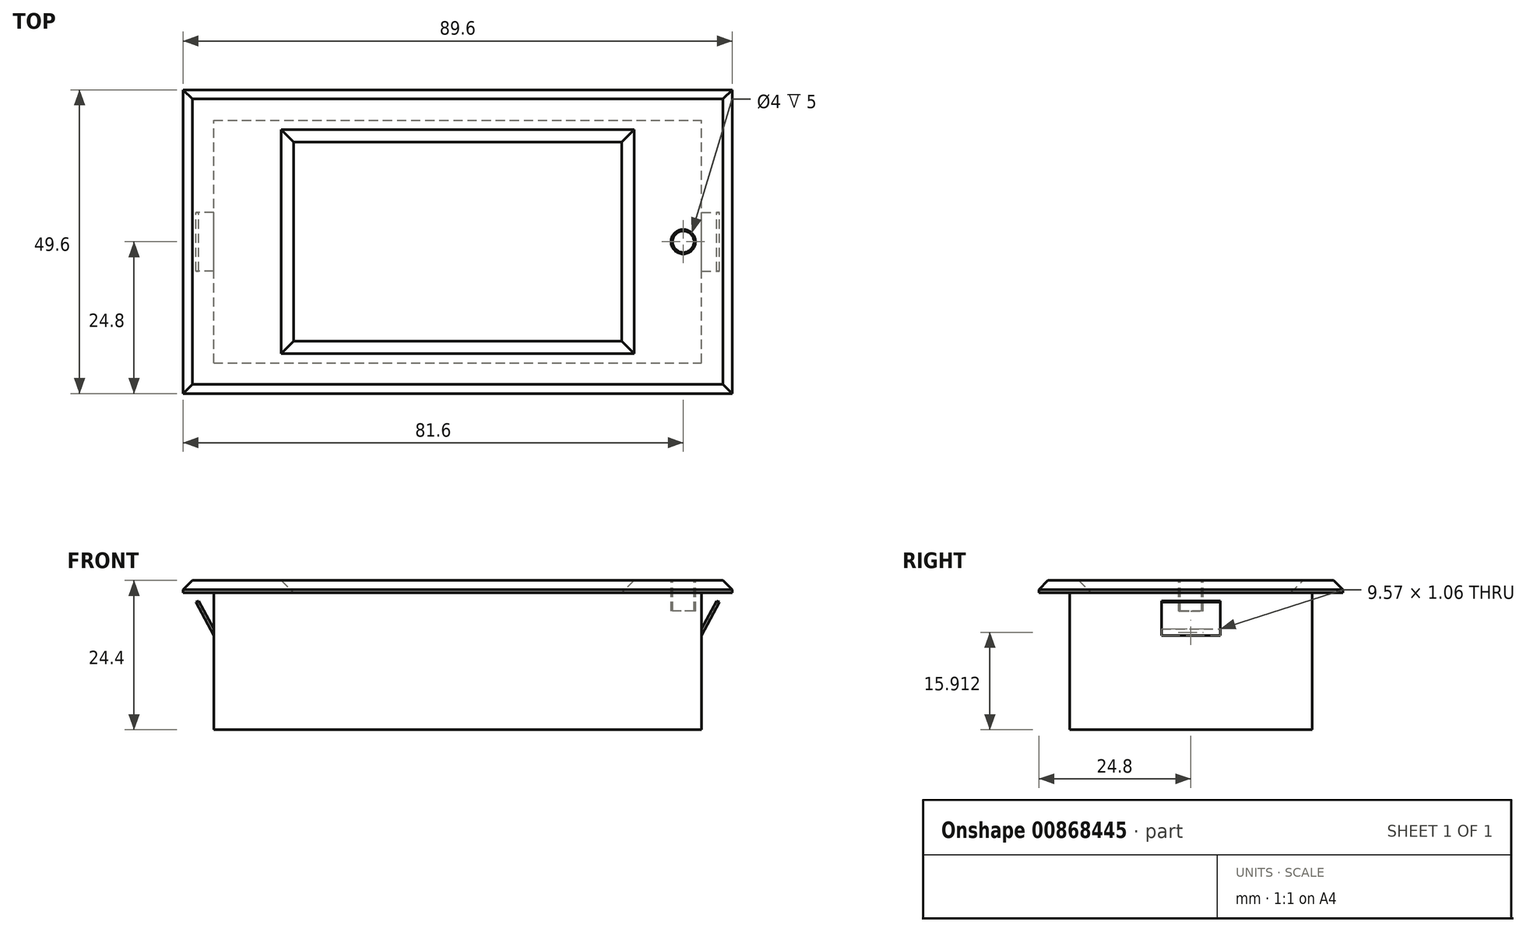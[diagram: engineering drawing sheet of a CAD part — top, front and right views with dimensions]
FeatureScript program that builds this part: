
annotation { "Feature Type Name" : "Feature", "Feature Type Description" : "" }
export const myFeature = defineFeature(function(context is Context, id is Id, definition is map)
    precondition{}
    {
        {
            var Q0;
            Q0=qCreatedBy(makeId("Top.planeOp"),FACE);
            var sketch = newSketch(context, id + "F0", { "sketchPlane" : qUnion([Q0])});
            skLineSegment(sketch, "E0.bottom", {"start": v(0, 0) * mm, "end": v(89.6, 0) * mm});
            skLineSegment(sketch, "E0.top", {"start": v(0, 49.6) * mm, "end": v(89.6, 49.6) * mm});
            skLineSegment(sketch, "E0.left", {"start": v(0, 0) * mm, "end": v(0, 49.6) * mm});
            skLineSegment(sketch, "E0.right", {"start": v(89.6, 0) * mm, "end": v(89.6, 49.6) * mm});
            skLineSegment(sketch, "E1.0", {"start": v(5, 5) * mm, "end": v(5, 44.6) * mm});
            skLineSegment(sketch, "E1.1", {"start": v(5, 5) * mm, "end": v(84.6, 5) * mm});
            skLineSegment(sketch, "E1.2", {"start": v(84.6, 5) * mm, "end": v(84.6, 44.6) * mm});
            skLineSegment(sketch, "E1.3", {"start": v(5, 44.6) * mm, "end": v(84.6, 44.6) * mm});
            skLineSegment(sketch, "E2", {"start": v(44.8, 49.6) * mm, "end": v(44.8, 0) * mm, "construction": true});
            skLineSegment(sketch, "E3", {"start": v(89.6, 24.8) * mm, "end": v(0, 24.8) * mm, "construction": true});
            skLineSegment(sketch, "E4.bottom", {"start": v(19.3, 39.8) * mm, "end": v(70.3, 39.8) * mm});
            skLineSegment(sketch, "E4.top", {"start": v(19.3, 9.8) * mm, "end": v(70.3, 9.8) * mm});
            skLineSegment(sketch, "E4.left", {"start": v(19.3, 39.8) * mm, "end": v(19.3, 9.8) * mm});
            skLineSegment(sketch, "E4.right", {"start": v(70.3, 39.8) * mm, "end": v(70.3, 9.8) * mm});
            skPoint(sketch, "E4.middle", {"position": v(44.8, 24.8) * mm});
            skSolve(sketch);
        }
        {
            var Q0;
            Q0=makeQuery(id+"F0.imprint","IMPRINT",FACE,{"disambiguationData":[TD([[makeQuery(id+"F0.imprint","IMPRINT",EDGE,{"derivedFrom":sQuery(id+"F0.wireOp",EDGE,"E1.0")}),-1.0]])]});
            var Q1;
            Q1=makeQuery(id+"F0.imprint","IMPRINT",FACE,{"disambiguationData":[TD([[makeQuery(id+"F0.imprint","IMPRINT",EDGE,{"derivedFrom":sQuery(id+"F0.wireOp",EDGE,"E4.bottom")}),-1.0]])]});
            extrude(context, id + "F1", {"entities" : qUnion([Q0, Q1]), "oppositeDirection" : true, "depth" : (24.4 - 2.05) * mm, "offsetDistance" : 25 * mm});
        }
        {
            var Q0;
            Q0=makeQuery(id+"F0.imprint","IMPRINT",FACE,{"disambiguationData":[TD([[makeQuery(id+"F0.imprint","IMPRINT",EDGE,{"derivedFrom":sQuery(id+"F0.wireOp",EDGE,"E0.bottom")}),1.0]])]});
            var Q1;
            Q1=makeQuery(id+"F0.imprint","IMPRINT",FACE,{"disambiguationData":[TD([[makeQuery(id+"F0.imprint","IMPRINT",EDGE,{"derivedFrom":sQuery(id+"F0.wireOp",EDGE,"E1.0")}),-1.0]])]});
            extrude(context, id + "F2", {"entities" : qUnion([Q0, Q1]), "operationType" : NewBodyOperationType.ADD, "depth" : 2.05 * mm, "offsetDistance" : 25 * mm});
        }
        {
            var Q0;
            Q0=qCreatedBy(makeId("Front.planeOp"),FACE);
            cPlane(context, id + "F3", {"entities" : qUnion([Q0]), "cplaneType" : CPlaneType.OFFSET, "offset" : (49.6 / 2) * mm, "oppositeDirection" : true, "width" : 150 * mm, "height" : 150 * mm});
        }
        {
            var Q0;
            Q0=qCreatedBy(id+"F3.planeOp",FACE);
            var sketch = newSketch(context, id + "F4", { "sketchPlane" : qUnion([Q0])});
            skLineSegment(sketch, "E5.0.0", {"start": v(84.6, 0) * mm, "end": v(5, 0) * mm});
            skLineSegment(sketch, "E5.0.1", {"start": v(5, 0) * mm, "end": v(5, -22.35) * mm});
            skLineSegment(sketch, "E5.0.2", {"start": v(5, -22.35) * mm, "end": v(84.6, -22.35) * mm});
            skLineSegment(sketch, "E5.0.3", {"start": v(84.6, -22.35) * mm, "end": v(84.6, 0) * mm});
            skLineSegment(sketch, "E6", {"start": v(5, -6.97) * mm, "end": v(84.6, -6.97) * mm});
            skLineSegment(sketch, "E7", {"start": v(44.8, 0) * mm, "end": v(44.8, -22.35) * mm, "construction": true});
            skLineSegment(sketch, "E8", {"start": v(5, -6.97) * mm, "end": v(2.1, -1.52) * mm});
            skLineSegment(sketch, "E9", {"start": v(2.1, -1.52) * mm, "end": v(5, -1.52) * mm, "construction": true});
            skLineSegment(sketch, "E10.0", {"start": v(5, -5.9) * mm, "end": v(2.54, -1.29) * mm});
            skLineSegment(sketch, "E11", {"start": v(2.1, -1.52) * mm, "end": v(2.54, -1.29) * mm});
            skLineSegment(sketch, "E12.MirrorCS", {"start": v(84.6, -6.97) * mm, "end": v(87.5, -1.52) * mm});
            skLineSegment(sketch, "E13.MirrorCS", {"start": v(84.6, -5.9) * mm, "end": v(87.06, -1.29) * mm});
            skLineSegment(sketch, "E14.MirrorCS", {"start": v(87.5, -1.52) * mm, "end": v(87.06, -1.29) * mm});
            skSolve(sketch);
        }
        {
            var Q0;
            {var subQ0=sQuery(id+"F4.wireOp",EDGE,"E8");Q0=makeQuery(id+"F4.imprint","IMPRINT",FACE,{"disambiguationData":[TD([[makeQuery(id+"F4.imprint","IMPRINT",EDGE,{"derivedFrom":subQ0}),-1.0]])]});}
            var Q1;
            {var subQ0=sQuery(id+"F4.wireOp",EDGE,"E12.MirrorCS");Q1=makeQuery(id+"F4.imprint","IMPRINT",FACE,{"disambiguationData":[TD([[makeQuery(id+"F4.imprint","IMPRINT",EDGE,{"derivedFrom":subQ0}),1.0]])]});}
            extrude(context, id + "F5", {"entities" : qUnion([Q0, Q1]), "operationType" : NewBodyOperationType.ADD, "depth" : 9.57 * mm, "offsetDistance" : 25 * mm, "symmetric" : true});
        }
        {
            var Q0;
            Q0=makeQuery(id+"F2.opExtrude","CAP_EDGE",EDGE,{"disambiguationData":[OSD([sQuery(id+"F0.wireOp",EDGE,"E0.left")])],"isStart":false});
            var Q1;
            Q1=makeQuery(id+"F2.opExtrude","CAP_EDGE",EDGE,{"disambiguationData":[OSD([sQuery(id+"F0.wireOp",EDGE,"E0.right")])],"isStart":false});
            var Q2;
            Q2=makeQuery(id+"F2.opExtrude","CAP_EDGE",EDGE,{"disambiguationData":[OSD([sQuery(id+"F0.wireOp",EDGE,"E0.top")])],"isStart":false});
            var Q3;
            Q3=makeQuery(id+"F2.opExtrude","CAP_EDGE",EDGE,{"disambiguationData":[OSD([sQuery(id+"F0.wireOp",EDGE,"E0.bottom")])],"isStart":false});
            chamfer(context, id + "F6", {"entities" : qUnion([Q0, Q1, Q2, Q3]), "width" : 1.5 * mm, "tangentPropagation" : true});
        }
        {
            var Q0;
            Q0=makeQuery(id+"F2.opExtrude","CAP_EDGE",EDGE,{"disambiguationData":[OSD([sQuery(id+"F0.wireOp",EDGE,"E4.bottom")])],"isStart":false});
            var Q1;
            Q1=makeQuery(id+"F2.opExtrude","CAP_EDGE",EDGE,{"disambiguationData":[OSD([sQuery(id+"F0.wireOp",EDGE,"E4.left")])],"isStart":false});
            var Q2;
            Q2=makeQuery(id+"F2.opExtrude","CAP_EDGE",EDGE,{"disambiguationData":[OSD([sQuery(id+"F0.wireOp",EDGE,"E4.top")])],"isStart":false});
            var Q3;
            Q3=makeQuery(id+"F2.opExtrude","CAP_EDGE",EDGE,{"disambiguationData":[OSD([sQuery(id+"F0.wireOp",EDGE,"E4.right")])],"isStart":false});
            chamfer(context, id + "F7", {"entities" : qUnion([Q0, Q1, Q2, Q3]), "width" : 3.3 * mm, "tangentPropagation" : true});
        }
        {
            var Q0;
            Q0=makeQuery(id+"F2.opExtrude","CAP_FACE",FACE,{"disambiguationData":[OSD([sQuery(id+"F0.wireOp",EDGE,"E0.bottom"),sQuery(id+"F0.wireOp",EDGE,"E0.top"),sQuery(id+"F0.wireOp",EDGE,"E0.left"),sQuery(id+"F0.wireOp",EDGE,"E0.right"),sQuery(id+"F0.wireOp",EDGE,"E4.bottom"),sQuery(id+"F0.wireOp",EDGE,"E4.top"),sQuery(id+"F0.wireOp",EDGE,"E4.left"),sQuery(id+"F0.wireOp",EDGE,"E4.right")])],"isStart":false});
            var sketch = newSketch(context, id + "F8", { "sketchPlane" : qUnion([Q0])});
            skLineSegment(sketch, "E15.0", {"start": v(89.6, 49.6) * mm, "end": v(89.6, 0) * mm});
            skCircle(sketch, "E16", {"center": v(81.6, 24.8) * mm, "radius": 2 * mm});
            skCircle(sketch, "E17.0", {"center": v(81.6, 24.8) * mm, "radius": 1.75 * mm});
            skPoint(sketch, "E18", {"position": v(89.6, 24.8) * mm});
            skSolve(sketch);
        }
        {
            var Q0;
            Q0=makeQuery(id+"F8.imprint","IMPRINT",FACE,{"disambiguationData":[TD([[makeQuery(id+"F8.imprint","IMPRINT",EDGE,{"derivedFrom":sQuery(id+"F8.wireOp",EDGE,"E16")}),1.0]])]});
            extrude(context, id + "F9", {"entities" : qUnion([Q0]), "operationType" : NewBodyOperationType.REMOVE, "oppositeDirection" : true, "depth" : 5 * mm, "offsetDistance" : 25 * mm});
        }
        {
            var Q0;
            Q0=makeQuery(id+"F1.opExtrude","CAP_FACE",FACE,{"disambiguationData":[OSD([sQuery(id+"F0.wireOp",EDGE,"E1.0"),sQuery(id+"F0.wireOp",EDGE,"E1.1"),sQuery(id+"F0.wireOp",EDGE,"E1.2"),sQuery(id+"F0.wireOp",EDGE,"E1.3")])],"isStart":true});
            var sketch = newSketch(context, id + "F10", { "sketchPlane" : qUnion([Q0])});
            skLineSegment(sketch, "E19.0.0", {"start": v(71.55, 8.55) * mm, "end": v(71.55, 41.05) * mm});
            skLineSegment(sketch, "E19.0.1", {"start": v(71.55, 41.05) * mm, "end": v(18.05, 41.05) * mm});
            skLineSegment(sketch, "E19.0.2", {"start": v(18.05, 41.05) * mm, "end": v(18.05, 8.55) * mm});
            skLineSegment(sketch, "E19.0.3", {"start": v(18.05, 8.55) * mm, "end": v(71.55, 8.55) * mm});
            skSolve(sketch);
        }
        {
            var Q0;
            Q0=makeQuery(id+"F10.imprint","IMPRINT",FACE,{"disambiguationData":[TD([[makeQuery(id+"F10.imprint","IMPRINT",EDGE,{"derivedFrom":sQuery(id+"F10.wireOp",EDGE,"E19.0.0")}),1.0]])]});
            extrude(context, id + "F11", {"entities" : qUnion([Q0]), "depth" : .1 * mm, "offsetDistance" : 25 * mm});
        }
    });
